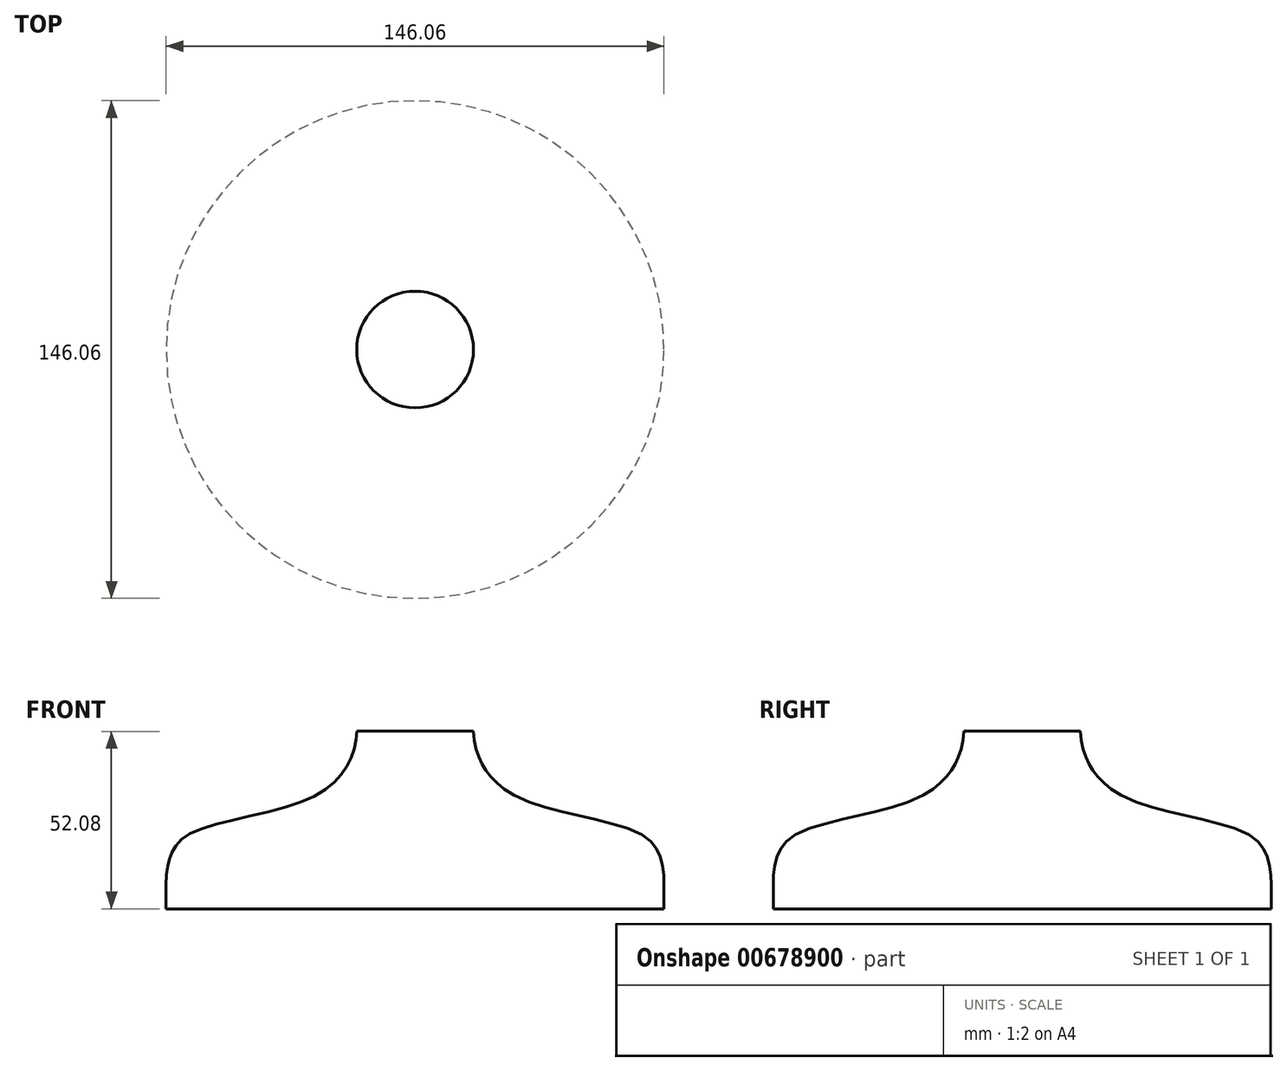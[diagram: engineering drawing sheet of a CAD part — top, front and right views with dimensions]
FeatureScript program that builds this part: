
annotation { "Feature Type Name" : "Feature", "Feature Type Description" : "" }
export const myFeature = defineFeature(function(context is Context, id is Id, definition is map)
    precondition{}
    {
        {
            var Q0;
            Q0=qCreatedBy(makeId("Front.planeOp"),FACE);
            var sketch = newSketch(context, id + "F0", { "sketchPlane" : qUnion([Q0])});
            skLineSegment(sketch, "E0", {"start": v(0, 0) * mm, "end": v(0, -74.93) * mm, "construction": true});
            skLineSegment(sketch, "E1", {"start": v(58.13, -24.81) * mm, "end": v(66.04, -23.7) * mm});
            skLineSegment(sketch, "E2", {"start": v(0, 0) * mm, "end": v(73.03, 0) * mm});
            skLineSegment(sketch, "E3", {"start": v(73.03, 0) * mm, "end": v(73.03, -15.64) * mm});
            skPoint(sketch, "E4.visualSharp", {"position": v(27.87, -75.65) * mm});
            skArc(sketch, "E4.filletArc", {"start": v(18.58, -75.06) * mm, "mid": v(25.06, -73.32) * mm, "end": v(28.19, -67.37) * mm});
            skPoint(sketch, "E5.visualSharp", {"position": v(27.87, -48.38) * mm});
            skArc(sketch, "E5.filletArc", {"start": v(36.42, -49.86) * mm, "mid": v(31.24, -52.35) * mm, "end": v(28.9, -57.6) * mm});
            skPoint(sketch, "E6.visualSharp", {"position": v(50.51, -47.29) * mm});
            skArc(sketch, "E6.filletArc", {"start": v(43.25, -49.17) * mm, "mid": v(48.6, -46.5) * mm, "end": v(50.8, -40.96) * mm});
            skPoint(sketch, "E7.visualSharp", {"position": v(54.25, -25.36) * mm});
            skArc(sketch, "E7.filletArc", {"start": v(58.13, -24.81) * mm, "mid": v(53.01, -27.57) * mm, "end": v(50.92, -32.99) * mm});
            skPoint(sketch, "E8.visualSharp", {"position": v(73.03, -22.7) * mm});
            skArc(sketch, "E8.filletArc", {"start": v(66.04, -23.7) * mm, "mid": v(71.03, -20.97) * mm, "end": v(73.03, -15.64) * mm});
            skArc(sketch, "E9.MirrorCS", {"start": v(-66.04, -23.7) * mm, "mid": v(-71.03, -20.97) * mm, "end": v(-73.03, -15.64) * mm});
            skLineSegment(sketch, "E10.MirrorCS", {"start": v(-58.13, -24.81) * mm, "end": v(-66.04, -23.7) * mm});
            skLineSegment(sketch, "E11.MirrorCS", {"start": v(-43.25, -49.17) * mm, "end": v(-36.42, -49.86) * mm});
            skArc(sketch, "E12.MirrorCS", {"start": v(-43.25, -49.17) * mm, "mid": v(-48.6, -46.5) * mm, "end": v(-50.8, -40.96) * mm});
            skArc(sketch, "E13.MirrorCS", {"start": v(-18.58, -75.06) * mm, "mid": v(-25.06, -73.32) * mm, "end": v(-28.19, -67.37) * mm});
            skArc(sketch, "E14.MirrorCS", {"start": v(-36.42, -49.86) * mm, "mid": v(-31.24, -52.35) * mm, "end": v(-28.9, -57.6) * mm});
            skArc(sketch, "E15.MirrorCS", {"start": v(-58.13, -24.81) * mm, "mid": v(-53.01, -27.57) * mm, "end": v(-50.92, -32.99) * mm});
            skPoint(sketch, "E16.MirrorP", {"position": v(-50.51, -47.29) * mm});
            skLineSegment(sketch, "E17.MirrorCS", {"start": v(-50.92, -32.99) * mm, "end": v(-50.8, -40.96) * mm});
            skPoint(sketch, "E18.MirrorP", {"position": v(-27.87, -48.38) * mm});
            skPoint(sketch, "E19.MirrorP", {"position": v(-27.87, -75.65) * mm});
            skLineSegment(sketch, "E20.MirrorCS", {"start": v(-73.03, 0) * mm, "end": v(-73.03, -15.64) * mm});
            skPoint(sketch, "E21.MirrorP", {"position": v(-73.03, -22.7) * mm});
            skLineSegment(sketch, "E22.MirrorCS", {"start": v(0, 0) * mm, "end": v(-73.03, 0) * mm});
            skPoint(sketch, "E23.MirrorP", {"position": v(-54.25, -25.36) * mm});
            skLineSegment(sketch, "E24", {"start": v(28.9, -57.6) * mm, "end": v(28.19, -67.37) * mm});
            skLineSegment(sketch, "E25.MirrorCS", {"start": v(-28.9, -57.6) * mm, "end": v(-28.19, -67.37) * mm});
            skPoint(sketch, "E26", {"position": v(43.25, -49.17) * mm});
            skLineSegment(sketch, "E27", {"start": v(50.92, -32.99) * mm, "end": v(50.8, -40.96) * mm});
            skLineSegment(sketch, "E28", {"start": v(36.42, -49.86) * mm, "end": v(43.25, -49.17) * mm});
            skArc(sketch, "E29", {"start": v(18.58, -75.06) * mm, "mid": v(9.31, -74) * mm, "end": v(0, -73.66) * mm});
            skArc(sketch, "E30.MirrorCS", {"start": v(-18.58, -75.06) * mm, "mid": v(-9.31, -74) * mm, "end": v(0, -73.66) * mm});
            skSolve(sketch);
        }
        {
            var Q0;
            Q0=makeQuery(id+"F0.imprint","IMPRINT",FACE,{"disambiguationData":[TD([[makeQuery(id+"F0.imprint","IMPRINT",EDGE,{"derivedFrom":sQuery(id+"F0.wireOp",EDGE,"E1")}),1.0]])]});
            var Q1;
            Q1=sQuery(id+"F0.wireOp",EDGE,"E8.filletArc");
            var Q2;
            Q2=sQuery(id+"F0.wireOp",EDGE,"E27");
            var Q3;
            Q3=sQuery(id+"F0.wireOp",EDGE,"E7.filletArc");
            var Q4;
            Q4=sQuery(id+"F0.wireOp",EDGE,"E5.filletArc");
            var Q5;
            Q5=sQuery(id+"F0.wireOp",EDGE,"E4.filletArc");
            var Q6;
            Q6=sQuery(id+"F0.wireOp",EDGE,"E3");
            var Q7;
            Q7=sQuery(id+"F0.wireOp",EDGE,"E2");
            var Q8;
            Q8=sQuery(id+"F0.wireOp",EDGE,"E28");
            var Q9;
            Q9=sQuery(id+"F0.wireOp",EDGE,"E29");
            var Q10;
            Q10=sQuery(id+"F0.wireOp",EDGE,"E1");
            var Q11;
            Q11=sQuery(id+"F0.wireOp",EDGE,"E6.filletArc");
            var Q12;
            Q12=sQuery(id+"F0.wireOp",EDGE,"E24");
            var Q13;
            Q13=sQuery(id+"F0.wireOp",EDGE,"E0");
            revolve(context, id + "F1", {"bodyType" : ToolBodyType.SURFACE, "entities" : qUnion([Q0]), "surfaceEntities" : qUnion([Q1, Q2, Q3, Q4, Q5, Q6, Q7, Q8, Q9, Q10, Q11, Q12]), "axis" : qUnion([Q13]), "revolveType" : RevolveType.SYMMETRIC, "oppositeDirection" : true, "angle" : 360 * degree, "surfaceOperationType" : NewSurfaceOperationType.NEW});
        }
        {
            var Q0;
            Q0=qCreatedBy(makeId("Front.planeOp"),FACE);
            var sketch = newSketch(context, id + "F2", { "sketchPlane" : qUnion([Q0])});
            skLineSegment(sketch, "E31", {"start": v(73.03, 0) * mm, "end": v(73.03, 7.11) * mm});
            skFitSpline(sketch, "E32", {"points": [v(73.03, 7.11) * mm, v(71.71, 15.73) * mm, v(65.49, 22.32) * mm, v(32.55, 31.68) * mm, v(19.75, 42.3) * mm, v(17.12, 52.08) * mm], "startDerivative": vector(-0.2, 72.17) * mm, "endDerivative": vector(-1.11, 57.04) * mm});
            skFitSpline(sketch, "E33.MirrorCS", {"points": [v(-73.03, 7.11) * mm, v(-71.71, 15.73) * mm, v(-65.49, 22.32) * mm, v(-32.55, 31.68) * mm, v(-19.75, 42.3) * mm, v(-17.12, 52.08) * mm], "startDerivative": vector(0.2, 72.17) * mm, "endDerivative": vector(1.11, 57.04) * mm});
            skLineSegment(sketch, "E34.MirrorCS", {"start": v(-73.03, 0) * mm, "end": v(-73.03, 7.11) * mm});
            skLineSegment(sketch, "E35", {"start": v(-17.12, 52.08) * mm, "end": v(17.12, 52.08) * mm});
            skLineSegment(sketch, "E36", {"start": v(-73.03, 0) * mm, "end": v(73.03, 0) * mm});
            skLineSegment(sketch, "E37", {"start": v(0, 52.08) * mm, "end": v(0, 0) * mm});
            skSolve(sketch);
        }
        {
            var Q0;
            Q0=makeQuery(id+"F2.imprint","IMPRINT",FACE,{"disambiguationData":[TD([[makeQuery(id+"F2.imprint","IMPRINT",EDGE,{"derivedFrom":sQuery(id+"F2.wireOp",EDGE,"E31")}),1.0]])]});
            var Q1;
            Q1=sQuery(id+"F2.wireOp",EDGE,"E37");
            revolve(context, id + "F3", {"surfaceOperationType" : NewSurfaceOperationType.NEW, "entities" : qUnion([Q0]), "axis" : qUnion([Q1]), "revolveType" : RevolveType.FULL, "oppositeDirection" : true});
        }
    });
